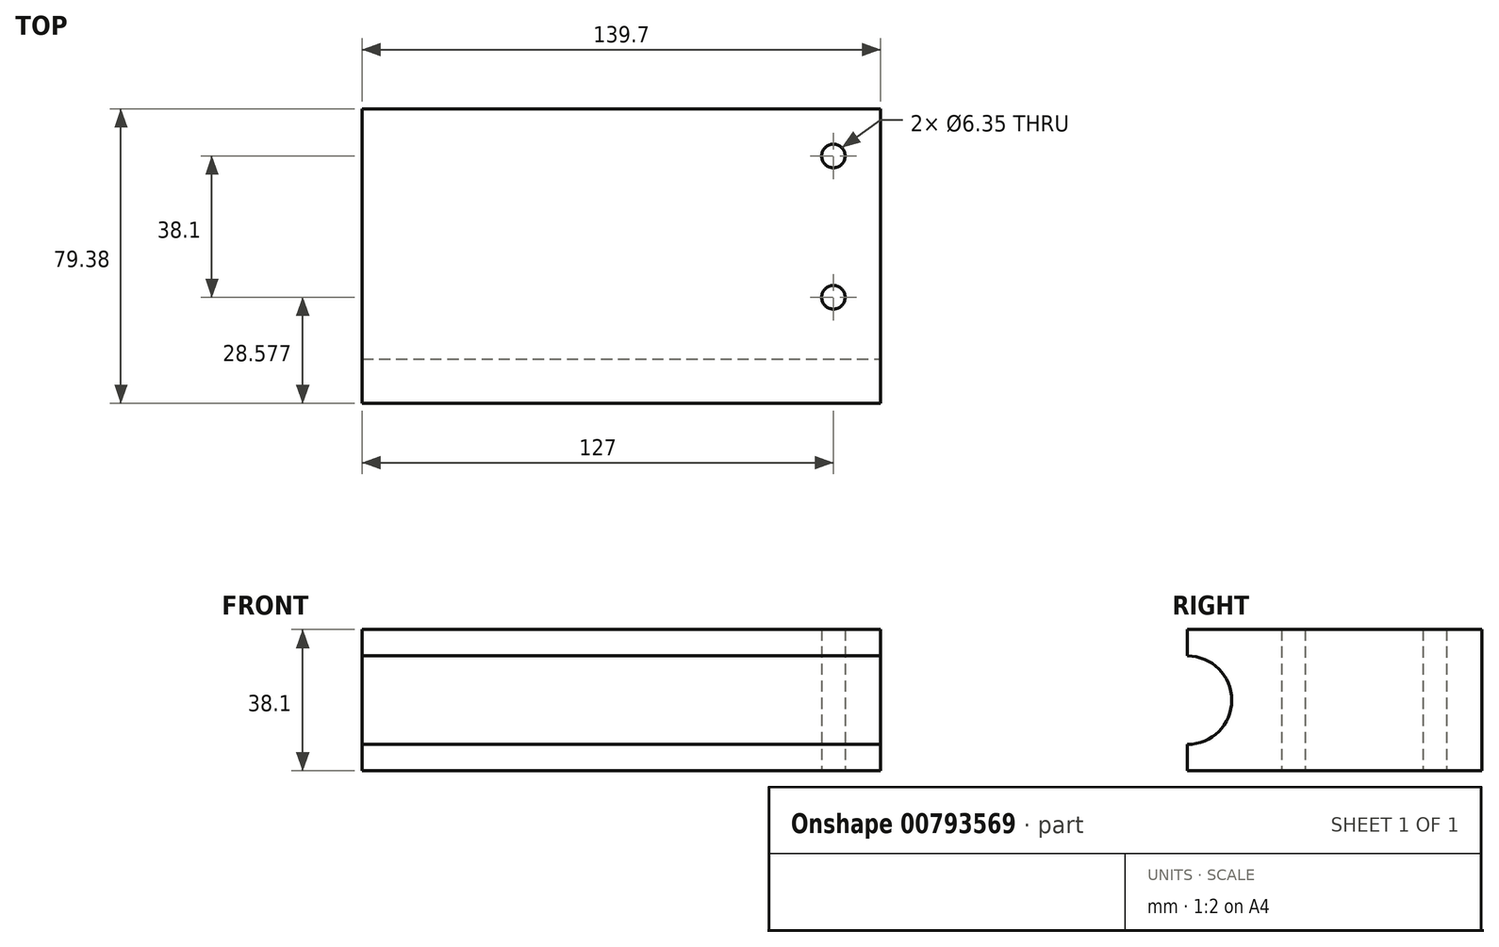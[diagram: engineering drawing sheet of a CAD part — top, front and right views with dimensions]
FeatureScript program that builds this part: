
annotation { "Feature Type Name" : "Feature", "Feature Type Description" : "" }
export const myFeature = defineFeature(function(context is Context, id is Id, definition is map)
    precondition{}
    {
        {
            var Q0;
            Q0=qCreatedBy(makeId("Top.planeOp"),FACE);
            var sketch = newSketch(context, id + "F0", { "sketchPlane" : qUnion([Q0])});
            skLineSegment(sketch, "E0.bottom", {"start": v(-69.85, 39.69) * mm, "end": v(69.85, 39.69) * mm});
            skLineSegment(sketch, "E0.top", {"start": v(-69.85, -39.69) * mm, "end": v(69.85, -39.69) * mm});
            skLineSegment(sketch, "E0.left", {"start": v(-69.85, 39.69) * mm, "end": v(-69.85, -39.69) * mm});
            skLineSegment(sketch, "E0.right", {"start": v(69.85, 39.69) * mm, "end": v(69.85, -39.69) * mm});
            skPoint(sketch, "E0.middle", {"position": v(0, 0) * mm});
            skCircle(sketch, "E1", {"center": v(57.15, 26.99) * mm, "radius": 3.18 * mm});
            skCircle(sketch, "E2", {"center": v(57.15, -11.11) * mm, "radius": 3.18 * mm});
            skSolve(sketch);
        }
        {
            var Q0;
            Q0=makeQuery(id+"F0.imprint","IMPRINT",FACE,{"disambiguationData":[TD([[makeQuery(id+"F0.imprint","IMPRINT",EDGE,{"derivedFrom":sQuery(id+"F0.wireOp",EDGE,"E0.bottom")}),-1.0]])]});
            extrude(context, id + "F1", {"entities" : qUnion([Q0]), "depth" : 38.1 * mm, "offsetDistance" : 25.4 * mm});
        }
        {
            var Q0;
            Q0=makeQuery(id+"F1.opExtrude","SWEPT_FACE",FACE,{"disambiguationData":[OSD([sQuery(id+"F0.wireOp",EDGE,"E0.right")])]});
            var sketch = newSketch(context, id + "F2", { "sketchPlane" : qUnion([Q0])});
            skCircle(sketch, "E3", {"center": v(-39.69, 19.05) * mm, "radius": 11.91 * mm});
            skSolve(sketch);
        }
        {
            var Q0;
            {var subQ0=sQuery(id+"F2.wireOp",EDGE,"E3");var subQ1=makeQuery(id+"F1.opExtrude","SWEPT_EDGE",EDGE,{"disambiguationData":[OSD([sQuery(id+"F0.wireOp",EDGE,"E0.top"),sQuery(id+"F0.wireOp",EDGE,"E0.right")])]});var subQ2=makeQuery(id+"F2.imprint","INTERSECT",VERTEX,{"disambiguationData":[OD(0.0)],"derivedFrom":[subQ1,subQ0]});Q0=makeQuery(id+"F2.imprint","IMPRINT",FACE,{"disambiguationData":[TD([[makeQuery(id+"F2.imprint","IMPRINT",EDGE,{"disambiguationData":[TD([[subQ2,-1.0]])],"derivedFrom":subQ0}),1.0]])]});}
            extrude(context, id + "F3", {"entities" : qUnion([Q0]), "operationType" : NewBodyOperationType.REMOVE, "endBound" : BoundingType.THROUGH_ALL, "oppositeDirection" : true, "depth" : 25.4 * mm, "offsetDistance" : 25.4 * mm});
        }
    });
